# Revit family: frozen_counter_top_washbasin
name_source: partatom
category: Generic Models
units: mm (PartAtom-declared; Revit-internal decimal feet)

## family parameters
Always vertical = No
Can host rebar = No
Cut with Voids When Loaded = No
Part Type = Normal
Room Calculation Point = No
Round Connector Dimension = Use Diameter
Shared = No
Work Plane-Based = No

## types (1)
- Default
    BIMobject category = Basins
    BIMobject category code = sanitary-basins
    BIMobject main category = Sanitary
    BIMobject main category code = sanitary
    BOSUseNativeGeometries = 1
    Brand url = https://www.simas.it
    Default Elevation = 0' - 0"
    Design country = Italy
    Edition number = 1
    IFC Classification = Sanitary Terminal
    Installation instructions = https://www.simas.it
    Manufacturer country = Italy
    Manufacturer name = Simas
    Masterformat 2014 Code = 22 41 16.16
    Masterformat 2014 Description = Residential Sinks
    Material main = Ceramics
    NBS Reference Code = 35-65-70-94
    NBS Reference Description = Wash Basin Systems
    OmniClass Code = 23-31 13 00
    OmniClass Description = Sinks
    Product Guid = 911cac65-7fb9-49cf-bf93-0f4e19903d79
    Product SKU = fz12
    Product certification = https://www.simas.it
    Product data url = https://bimobject.com
    Product family = Basin
    Product group = Frozen
    Product name = Frozen - Counter top washbasin 100 - FZ12
    Product url = https://www.simas.it
    QR code = http://bimobject.com
    Technical description = https://www.simas.it
    UNSPSC Code = 301815
    Uniclass 1.4 Code = L7212
    Uniclass 1.4 Description = Washbasins
    Uniclass 2015 Code = Pr_40_20_96_15
    Uniclass 2015 Name = Ceramic sinks
    Uniformat II Code = C10
    Uniformat II Description = INTERIOR CONSTRUCTION
    Youtube clip = https://www.youtube.com
